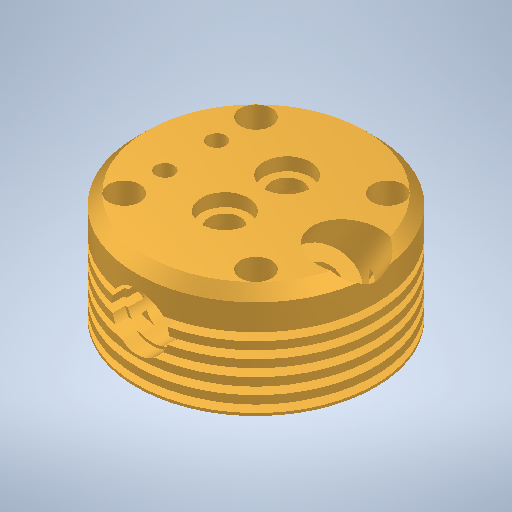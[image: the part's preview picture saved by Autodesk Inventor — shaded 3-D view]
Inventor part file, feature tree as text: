
AUTODESK INVENTOR PART (.ipt)
format: ipt  version: 2025 (Build 290162010, 162A)  size: 504,832 bytes
history: native  units: mm
features: sketch x9, plane x5, hole x5, revolve x4, pattern_circular x1, mirror x1, chamfer x1, projected_geometry x1
ambient origin geometry x8: Origin, YZ Plane, XZ Plane, XY Plane, X Axis, Y Axis, Z Axis, Center Point
bodies: Solid1 (feature_tree)
feature tree (27):
  revolve  "Revolution1"  [1 undecoded]
  plane  "Work Plane1"
  revolve  "Revolution2"  [1 undecoded]
  plane  "Work Plane10"
  hole  "Hole2"  [1 undecoded]
  hole  "Hole3"  [1 undecoded]
  pattern_circular  "Circular Pattern1"  [2 undecoded]
  plane  "Work Plane11"
  hole  "Hole4"  [1 undecoded]
  revolve  "Revolution4"  [1 undecoded]
  plane  "Work Plane6"
  hole  "Hole5"  [1 undecoded]
  mirror  "Mirror2"
  plane  "Work Plane7"
  revolve  "Revolution6"  [1 undecoded]
  chamfer  "Chamfer2"  Distance=36.0mm
  hole  "Hole6"  [1 undecoded]
  sketch  "Sketch1"  dims[d0=46.0mm d1=21.0mm]
  sketch  "Sketch3"  dims[d2=90.0deg d4=0.0mm]
  projected_geometry  "Projected Loop2"
  sketch  "Sketch12"  dims[d16=1.5mm d17=1.5mm]
  sketch  "Sketch13"  dims[d18=1.5mm d19=1.5mm]
  sketch  "Sketch14"  dims[d20=1.5mm]
  sketch  "Sketch16"  dims[d21=36.0mm]
  sketch  "Sketch18"  dims[d22=6.5mm]
  sketch  "Sketch20"  dims[d23=1.5mm]
  sketch  "Sketch22"  dims[d24=1.5mm d25=1.5mm d26=1.5mm d27=42.0mm d28=90.0deg d64=12.0mm d65=6.0mm d66=6.0mm d67=9.0mm d68=2.5mm d69=90.0deg d70=4.5mm d71=0.0mm d72=36.0mm d73=45.0deg d74=6.0mm d75=6.0mm d76=9.0mm d77=2.5mm d78=90.0deg d79=5.0mm d80=0.0mm d81=40.0mm d82=360.0deg d86=11.0mm d87=6.0mm d88=9.0mm d89=2.5mm d90=90.0deg d91=12.0mm d92=0.0mm d93=12.0mm d94=2.0mm d95=2.5mm d96=29.0mm d97=360.0deg d98=23.0mm d100=10.0mm d101=6.0mm d102=11.0mm d103=3.0mm d104=90.0deg d105=13.0mm d106=0.0mm d107=0.0mm d127=18.0mm d136=360.0deg d137=21.293017mm d138=12.0mm d139=6.0mm d140=0.0mm d141=-4.5mm d145=2.0mm d146=2.0mm d147=45.0deg d148=13.5mm d151=12.6mm d152=5.0mm d153=5.0mm d154=3.5mm d155=6.0mm d156=4.0mm d157=2.0mm d158=90.0deg d159=7.0mm d160=0.0mm d161=11.0mm]
note: 11 required parameter values undecoded (feature->parameter linkage not recoverable at this tier; creation-order binding heuristic only, values carry confidence <= 0.55)